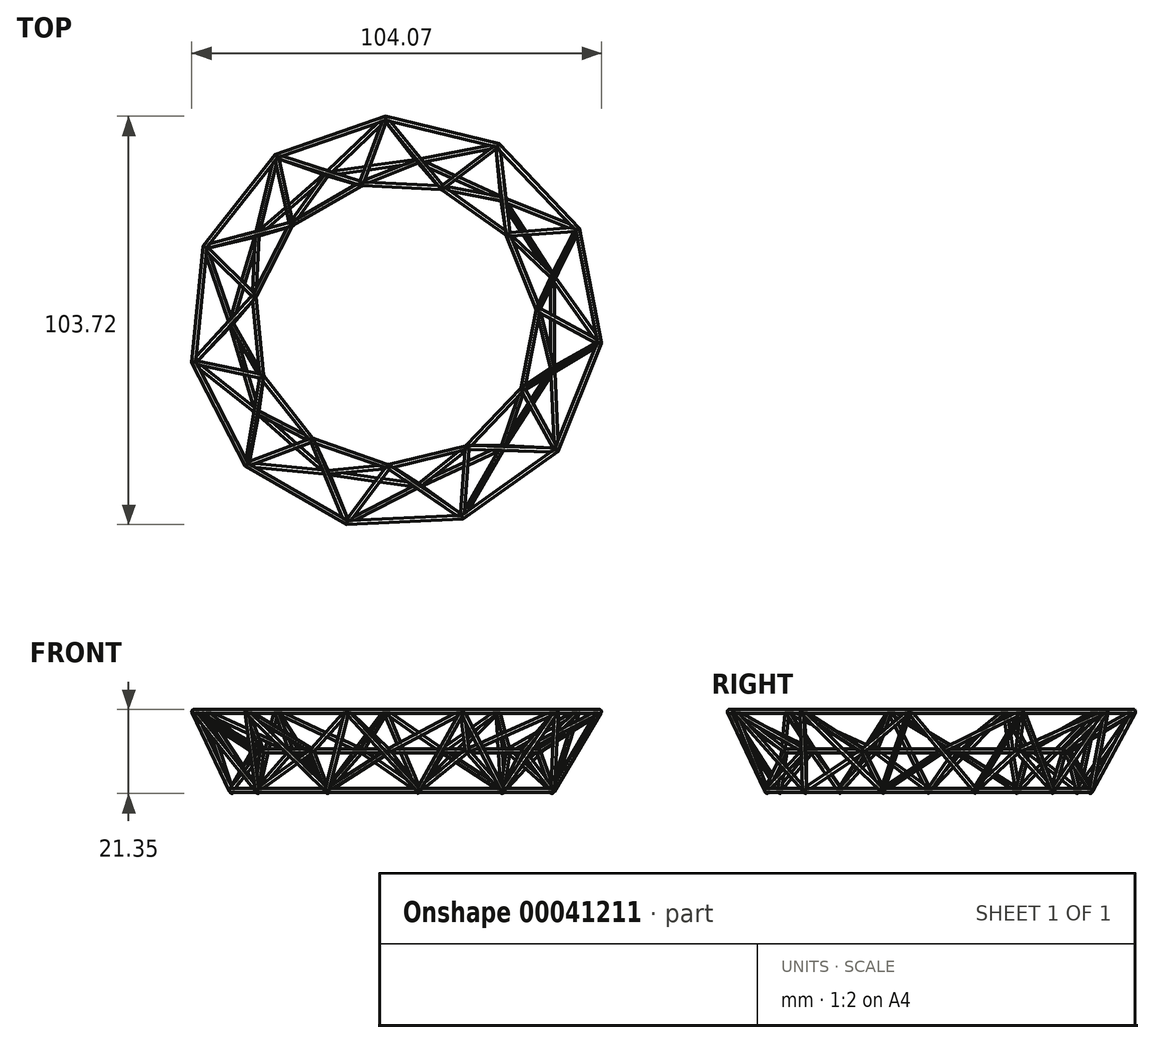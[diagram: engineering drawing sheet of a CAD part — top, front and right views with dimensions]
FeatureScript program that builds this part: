
annotation { "Feature Type Name" : "Feature", "Feature Type Description" : "" }
export const myFeature = defineFeature(function(context is Context, id is Id, definition is map)
    precondition{}
    {
        {
            var Q0;
            Q0=qCreatedBy(makeId("Front.planeOp"),FACE);
            var sketch = newSketch(context, id + "F0", { "sketchPlane" : qUnion([Q0])});
            skLineSegment(sketch, "E0", {"start": v(0, 0) * mm, "end": v(0, 400) * mm, "construction": true});
            skSolve(sketch);
        }
        {
            var Q0;
            Q0=qCreatedBy(makeId("Top.planeOp"),FACE);
            var sketch = newSketch(context, id + "F1", { "sketchPlane" : qUnion([Q0])});
            skCircle(sketch, "E1.cCircle", {"center": v(0, 0) * mm, "radius": 40 * mm, "construction": true});
            skLineSegment(sketch, "E1.0", {"start": v(40, 11.75) * mm, "end": v(40, -11.75) * mm});
            skLineSegment(sketch, "E1.1", {"start": v(40, -11.75) * mm, "end": v(27.3, -31.5) * mm});
            skLineSegment(sketch, "E1.2", {"start": v(27.3, -31.5) * mm, "end": v(5.93, -41.26) * mm});
            skLineSegment(sketch, "E1.3", {"start": v(5.93, -41.26) * mm, "end": v(-17.32, -37.92) * mm});
            skLineSegment(sketch, "E1.4", {"start": v(-17.32, -37.92) * mm, "end": v(-35.07, -22.54) * mm});
            skLineSegment(sketch, "E1.5", {"start": v(-35.07, -22.54) * mm, "end": v(-41.69, 0) * mm});
            skLineSegment(sketch, "E1.6", {"start": v(-41.69, 0) * mm, "end": v(-35.07, 22.54) * mm});
            skLineSegment(sketch, "E1.7", {"start": v(-35.07, 22.54) * mm, "end": v(-17.32, 37.92) * mm});
            skLineSegment(sketch, "E1.8", {"start": v(-17.32, 37.92) * mm, "end": v(5.93, 41.26) * mm});
            skLineSegment(sketch, "E1.9", {"start": v(5.93, 41.26) * mm, "end": v(27.3, 31.5) * mm});
            skLineSegment(sketch, "E1.10", {"start": v(27.3, 31.5) * mm, "end": v(40, 11.75) * mm});
            skPoint(sketch, "E1.0.midPoint", {"position": v(40, 0) * mm});
            skLineSegment(sketch, "E2", {"start": v(0, 0) * mm, "end": v(40, 0) * mm, "construction": true});
            skSolve(sketch);
        }
        {
            var Q0;
            Q0=sQuery(id+"F1.wireOp",VERTEX,"E1.0.midPoint");
            var Q1;
            Q1=sQuery(id+"F1.wireOp",EDGE,"E1.0");
            cPlane(context, id + "F2", {"entities" : qUnion([Q0, Q1]), "cplaneType" : CPlaneType.LINE_POINT, "offset" : 150 * mm, "width" : 150 * mm, "height" : 150 * mm});
        }
        {
            var Q0;
            Q0=qCreatedBy(id+"F2.planeOp",FACE);
            var sketch = newSketch(context, id + "F3", { "sketchPlane" : qUnion([Q0])});
            skCircle(sketch, "E3", {"center": v(40, 0) * mm, "radius": 0.5 * mm});
            skSolve(sketch);
        }
        {
            var Q0;
            Q0=makeQuery(id+"F3.imprint","IMPRINT",FACE,{"disambiguationData":[TD([[makeQuery(id+"F3.imprint","IMPRINT",EDGE,{"derivedFrom":sQuery(id+"F3.wireOp",EDGE,"E3")}),1.0]])]});
            var Q1;
            Q1 = qConstructionFilter(qBodyType(qCreatedBy(id + "F1" ,EDGE), BodyType.WIRE), ConstructionObject.NO);
            sweep(context, id + "F4", {"profiles" : qUnion([Q0]), "path" : qUnion([Q1])});
        }
        {
            var Q0;
            Q0=qCreatedBy(makeId("Top.planeOp"),FACE);
            cPlane(context, id + "F5", {"entities" : qUnion([Q0]), "cplaneType" : CPlaneType.OFFSET, "offset" : 10 * mm, "width" : 150 * mm, "height" : 150 * mm});
        }
        {
            var Q0;
            Q0=qCreatedBy(id+"F5.planeOp",FACE);
            var sketch = newSketch(context, id + "F6", { "sketchPlane" : qUnion([Q0])});
            skCircle(sketch, "E4.cCircle", {"center": v(0, 0) * mm, "radius": 35 * mm, "construction": true});
            skLineSegment(sketch, "E4.0", {"start": v(36.31, 3.47) * mm, "end": v(32.42, -16.72) * mm});
            skLineSegment(sketch, "E4.1", {"start": v(32.42, -16.72) * mm, "end": v(18.24, -31.6) * mm});
            skLineSegment(sketch, "E4.2", {"start": v(18.24, -31.6) * mm, "end": v(-1.74, -36.44) * mm});
            skLineSegment(sketch, "E4.3", {"start": v(-1.74, -36.44) * mm, "end": v(-21.16, -29.71) * mm});
            skLineSegment(sketch, "E4.4", {"start": v(-21.16, -29.71) * mm, "end": v(-33.86, -13.56) * mm});
            skLineSegment(sketch, "E4.5", {"start": v(-33.86, -13.56) * mm, "end": v(-35.82, 6.9) * mm});
            skLineSegment(sketch, "E4.6", {"start": v(-35.82, 6.9) * mm, "end": v(-26.4, 25.17) * mm});
            skLineSegment(sketch, "E4.7", {"start": v(-26.4, 25.17) * mm, "end": v(-8.6, 35.45) * mm});
            skLineSegment(sketch, "E4.8", {"start": v(-8.6, 35.45) * mm, "end": v(11.93, 34.47) * mm});
            skLineSegment(sketch, "E4.9", {"start": v(11.93, 34.47) * mm, "end": v(28.67, 22.55) * mm});
            skLineSegment(sketch, "E4.10", {"start": v(28.67, 22.55) * mm, "end": v(36.31, 3.47) * mm});
            skPoint(sketch, "E4.0.midPoint", {"position": v(34.37, -6.62) * mm});
            skLineSegment(sketch, "E5", {"start": v(0, 0) * mm, "end": v(34.37, -6.62) * mm, "construction": true});
            skSolve(sketch);
        }
        {
            var Q0;
            Q0=sQuery(id+"F6.wireOp",VERTEX,"E4.0.midPoint");
            var Q1;
            Q1=sQuery(id+"F6.wireOp",EDGE,"E4.0");
            cPlane(context, id + "F7", {"entities" : qUnion([Q0, Q1]), "cplaneType" : CPlaneType.LINE_POINT, "offset" : 150 * mm, "width" : 150 * mm, "height" : 150 * mm});
        }
        {
            var Q0;
            Q0=qCreatedBy(id+"F7.planeOp",FACE);
            var sketch = newSketch(context, id + "F8", { "sketchPlane" : qUnion([Q0])});
            skCircle(sketch, "E6", {"center": v(35, 10) * mm, "radius": 0.5 * mm});
            skSolve(sketch);
        }
        {
            var Q0;
            Q0=makeQuery(id+"F8.imprint","IMPRINT",FACE,{"disambiguationData":[TD([[makeQuery(id+"F8.imprint","IMPRINT",EDGE,{"derivedFrom":sQuery(id+"F8.wireOp",EDGE,"E6")}),1.0]])]});
            var Q1;
            Q1 = qConstructionFilter(qBodyType(qCreatedBy(id + "F6" ,EDGE), BodyType.WIRE), ConstructionObject.NO);
            sweep(context, id + "F9", {"profiles" : qUnion([Q0]), "path" : qUnion([Q1])});
        }
        {
            var Q0;
            Q0=qCreatedBy(makeId("Top.planeOp"),FACE);
            cPlane(context, id + "F10", {"entities" : qUnion([Q0]), "cplaneType" : CPlaneType.OFFSET, "offset" : 20 * mm, "width" : 150 * mm, "height" : 150 * mm});
        }
        {
            var Q0;
            Q0=qCreatedBy(id+"F10.planeOp",FACE);
            var sketch = newSketch(context, id + "F11", { "sketchPlane" : qUnion([Q0])});
            skCircle(sketch, "E7.cCircle", {"center": v(0, 0) * mm, "radius": 50 * mm, "construction": true});
            skLineSegment(sketch, "E7.0", {"start": v(46.32, 23.88) * mm, "end": v(51.87, -4.95) * mm});
            skLineSegment(sketch, "E7.1", {"start": v(51.87, -4.95) * mm, "end": v(40.96, -32.21) * mm});
            skLineSegment(sketch, "E7.2", {"start": v(40.96, -32.21) * mm, "end": v(17.04, -49.24) * mm});
            skLineSegment(sketch, "E7.3", {"start": v(17.04, -49.24) * mm, "end": v(-12.29, -50.64) * mm});
            skLineSegment(sketch, "E7.4", {"start": v(-12.29, -50.64) * mm, "end": v(-37.71, -35.96) * mm});
            skLineSegment(sketch, "E7.5", {"start": v(-37.71, -35.96) * mm, "end": v(-51.17, -9.86) * mm});
            skLineSegment(sketch, "E7.6", {"start": v(-51.17, -9.86) * mm, "end": v(-48.38, 19.37) * mm});
            skLineSegment(sketch, "E7.7", {"start": v(-48.38, 19.37) * mm, "end": v(-30.23, 42.45) * mm});
            skLineSegment(sketch, "E7.8", {"start": v(-30.23, 42.45) * mm, "end": v(-2.48, 52.05) * mm});
            skLineSegment(sketch, "E7.9", {"start": v(-2.48, 52.05) * mm, "end": v(26.06, 45.13) * mm});
            skLineSegment(sketch, "E7.10", {"start": v(26.06, 45.13) * mm, "end": v(46.32, 23.88) * mm});
            skPoint(sketch, "E7.0.midPoint", {"position": v(49.1, 9.46) * mm});
            skLineSegment(sketch, "E8", {"start": v(0, 0) * mm, "end": v(49.1, 9.46) * mm, "construction": true});
            skSolve(sketch);
        }
        {
            var Q0;
            Q0=sQuery(id+"F11.wireOp",VERTEX,"E7.0.midPoint");
            var Q1;
            Q1=sQuery(id+"F11.wireOp",EDGE,"E7.0");
            cPlane(context, id + "F12", {"entities" : qUnion([Q0, Q1]), "cplaneType" : CPlaneType.LINE_POINT, "offset" : 150 * mm, "width" : 150 * mm, "height" : 150 * mm});
        }
        {
            var Q0;
            Q0=qCreatedBy(id+"F12.planeOp",FACE);
            var sketch = newSketch(context, id + "F13", { "sketchPlane" : qUnion([Q0])});
            skCircle(sketch, "E9", {"center": v(50, 20) * mm, "radius": 0.5 * mm});
            skSolve(sketch);
        }
        {
            var Q0;
            Q0=makeQuery(id+"F13.imprint","IMPRINT",FACE,{"disambiguationData":[TD([[makeQuery(id+"F13.imprint","IMPRINT",EDGE,{"derivedFrom":sQuery(id+"F13.wireOp",EDGE,"E9")}),1.0]])]});
            var Q1;
            Q1 = qConstructionFilter(qBodyType(qCreatedBy(id + "F11" ,EDGE), BodyType.WIRE), ConstructionObject.NO);
            sweep(context, id + "F14", {"profiles" : qUnion([Q0]), "path" : qUnion([Q1])});
        }
        {
            var Q0;
            Q0=sQuery(id+"F1.wireOp",VERTEX,"E1.10.end");
            var Q1;
            Q1=sQuery(id+"F6.wireOp",VERTEX,"E4.0.start");
            var Q2;
            Q2=sQuery(id+"F1.wireOp",VERTEX,"E1.1.start");
            cPlane(context, id + "F15", {"entities" : qUnion([Q0, Q1, Q2]), "cplaneType" : CPlaneType.THREE_POINT, "offset" : 150 * mm, "width" : 150 * mm, "height" : 150 * mm});
        }
        {
            var Q0;
            Q0=qCreatedBy(id+"F15.planeOp",FACE);
            var sketch = newSketch(context, id + "F16", { "sketchPlane" : qUnion([Q0])});
            skLineSegment(sketch, "E10", {"start": v(-11.75, -13.84) * mm, "end": v(-3.47, -3.18) * mm});
            skLineSegment(sketch, "E11", {"start": v(-3.47, -3.18) * mm, "end": v(11.75, -13.84) * mm});
            skSolve(sketch);
        }
        {
            var Q0;
            Q0=sQuery(id+"F16.wireOp",EDGE,"E10");
            var Q1;
            Q1=sQuery(id+"F16.wireOp",VERTEX,"E10.start");
            cPlane(context, id + "F17", {"entities" : qUnion([Q0, Q1]), "cplaneType" : CPlaneType.LINE_POINT, "offset" : 150 * mm, "width" : 150 * mm, "height" : 150 * mm});
        }
        {
            var Q0;
            Q0=qCreatedBy(id+"F17.planeOp",FACE);
            var sketch = newSketch(context, id + "F18", { "sketchPlane" : qUnion([Q0])});
            skCircle(sketch, "E12", {"center": v(36.43, 9.05) * mm, "radius": 0.5 * mm});
            skSolve(sketch);
        }
        {
            var Q0;
            Q0 = qSketchRegion(id + "F18", true);
            var Q1;
            Q1 = qConstructionFilter(qBodyType(qCreatedBy(id + "F16" ,EDGE), BodyType.WIRE), ConstructionObject.NO);
            sweep(context, id + "F19", {"profiles" : qUnion([Q0]), "path" : qUnion([Q1])});
        }
        {
            var Q0;
            Q0=sQuery(id+"F11.wireOp",VERTEX,"E7.10.end");
            var Q1;
            Q1=sQuery(id+"F11.wireOp",VERTEX,"E7.1.start");
            var Q2;
            Q2=sQuery(id+"F1.wireOp",VERTEX,"E1.10.end");
            cPlane(context, id + "F20", {"entities" : qUnion([Q0, Q1, Q2]), "cplaneType" : CPlaneType.THREE_POINT, "offset" : 150 * mm, "width" : 150 * mm, "height" : 150 * mm});
        }
        {
            var Q0;
            Q0=qCreatedBy(id+"F20.planeOp",FACE);
            var sketch = newSketch(context, id + "F21", { "sketchPlane" : qUnion([Q0])});
            skLineSegment(sketch, "E13", {"start": v(-17.5, 36.75) * mm, "end": v(-5.17, 15.89) * mm});
            skLineSegment(sketch, "E14", {"start": v(-5.17, 15.89) * mm, "end": v(11.79, 38.96) * mm});
            skSolve(sketch);
        }
        {
            var Q0;
            Q0=sQuery(id+"F21.wireOp",VERTEX,"E13.start");
            var Q1;
            Q1=sQuery(id+"F21.wireOp",EDGE,"E13");
            cPlane(context, id + "F22", {"entities" : qUnion([Q0, Q1]), "cplaneType" : CPlaneType.LINE_POINT, "offset" : 150 * mm, "width" : 150 * mm, "height" : 150 * mm});
        }
        {
            var Q0;
            Q0=qCreatedBy(id+"F22.planeOp",FACE);
            var sketch = newSketch(context, id + "F23", { "sketchPlane" : qUnion([Q0])});
            skCircle(sketch, "E15", {"center": v(37.03, -10.04) * mm, "radius": 0.5 * mm});
            skSolve(sketch);
        }
        {
            var Q0;
            Q0 = qSketchRegion(id + "F23", true);
            var Q1;
            Q1 = qConstructionFilter(qBodyType(qCreatedBy(id + "F21" ,EDGE), BodyType.WIRE), ConstructionObject.NO);
            sweep(context, id + "F24", {"profiles" : qUnion([Q0]), "path" : qUnion([Q1])});
        }
        {
            var Q0;
            Q0=sQuery(id+"F11.wireOp",VERTEX,"E7.10.end");
            var Q1;
            Q1=sQuery(id+"F11.wireOp",VERTEX,"E7.1.start");
            var Q2;
            Q2=sQuery(id+"F6.wireOp",VERTEX,"E4.0.start");
            cPlane(context, id + "F25", {"entities" : qUnion([Q0, Q1, Q2]), "cplaneType" : CPlaneType.THREE_POINT, "offset" : 150 * mm, "width" : 150 * mm, "height" : 150 * mm});
        }
        {
            var Q0;
            Q0=qCreatedBy(id+"F25.planeOp",FACE);
            var sketch = newSketch(context, id + "F26", { "sketchPlane" : qUnion([Q0])});
            skLineSegment(sketch, "E16", {"start": v(47.34, 26.4) * mm, "end": v(35.06, 4.8) * mm});
            skLineSegment(sketch, "E17", {"start": v(35.06, 4.8) * mm, "end": v(54.15, -2.17) * mm});
            skSolve(sketch);
        }
        {
            var Q0;
            Q0=sQuery(id+"F26.wireOp",VERTEX,"E16.start");
            var Q1;
            Q1=sQuery(id+"F26.wireOp",EDGE,"E16");
            cPlane(context, id + "F27", {"entities" : qUnion([Q0, Q1]), "cplaneType" : CPlaneType.LINE_POINT, "offset" : 150 * mm, "width" : 150 * mm, "height" : 150 * mm});
        }
        {
            var Q0;
            Q0=qCreatedBy(id+"F27.planeOp",FACE);
            var sketch = newSketch(context, id + "F28", { "sketchPlane" : qUnion([Q0])});
            skCircle(sketch, "E18", {"center": v(30.2, 7.45) * mm, "radius": 0.5 * mm});
            skSolve(sketch);
        }
        {
            var Q0;
            Q0 = qSketchRegion(id + "F28", true);
            var Q1;
            Q1 = qConstructionFilter(qBodyType(qCreatedBy(id + "F26" ,EDGE), BodyType.WIRE), ConstructionObject.NO);
            sweep(context, id + "F29", {"profiles" : qUnion([Q0]), "path" : qUnion([Q1])});
        }
        {
            var Q0;
            Q0=makeQuery(id+"F19.opSweep","SWEPT_BODY",BODY,{"disambiguationData":[OSD([sQuery(id+"F16.wireOp",EDGE,"E11"),sQuery(id+"F18.wireOp",EDGE,"E12")])]});
            var Q1;
            Q1=makeQuery(id+"F24.opSweep","SWEPT_BODY",BODY,{"disambiguationData":[OSD([sQuery(id+"F21.wireOp",EDGE,"E14"),sQuery(id+"F23.wireOp",EDGE,"E15")])]});
            var Q2;
            Q2=makeQuery(id+"F29.opSweep","SWEPT_BODY",BODY,{"disambiguationData":[OSD([sQuery(id+"F26.wireOp",EDGE,"E17"),sQuery(id+"F28.wireOp",EDGE,"E18")])]});
            var Q3;
            Q3=sQuery(id+"F0.wireOp",EDGE,"E0");
            circularPattern(context, id + "F30", {"operationType" : NewBodyOperationType.ADD, "entities" : qUnion([Q0, Q1, Q2]), "axis" : qUnion([Q3]), "angle" : 32.73 * degree, "instanceCount" : 11});
        }
    });
